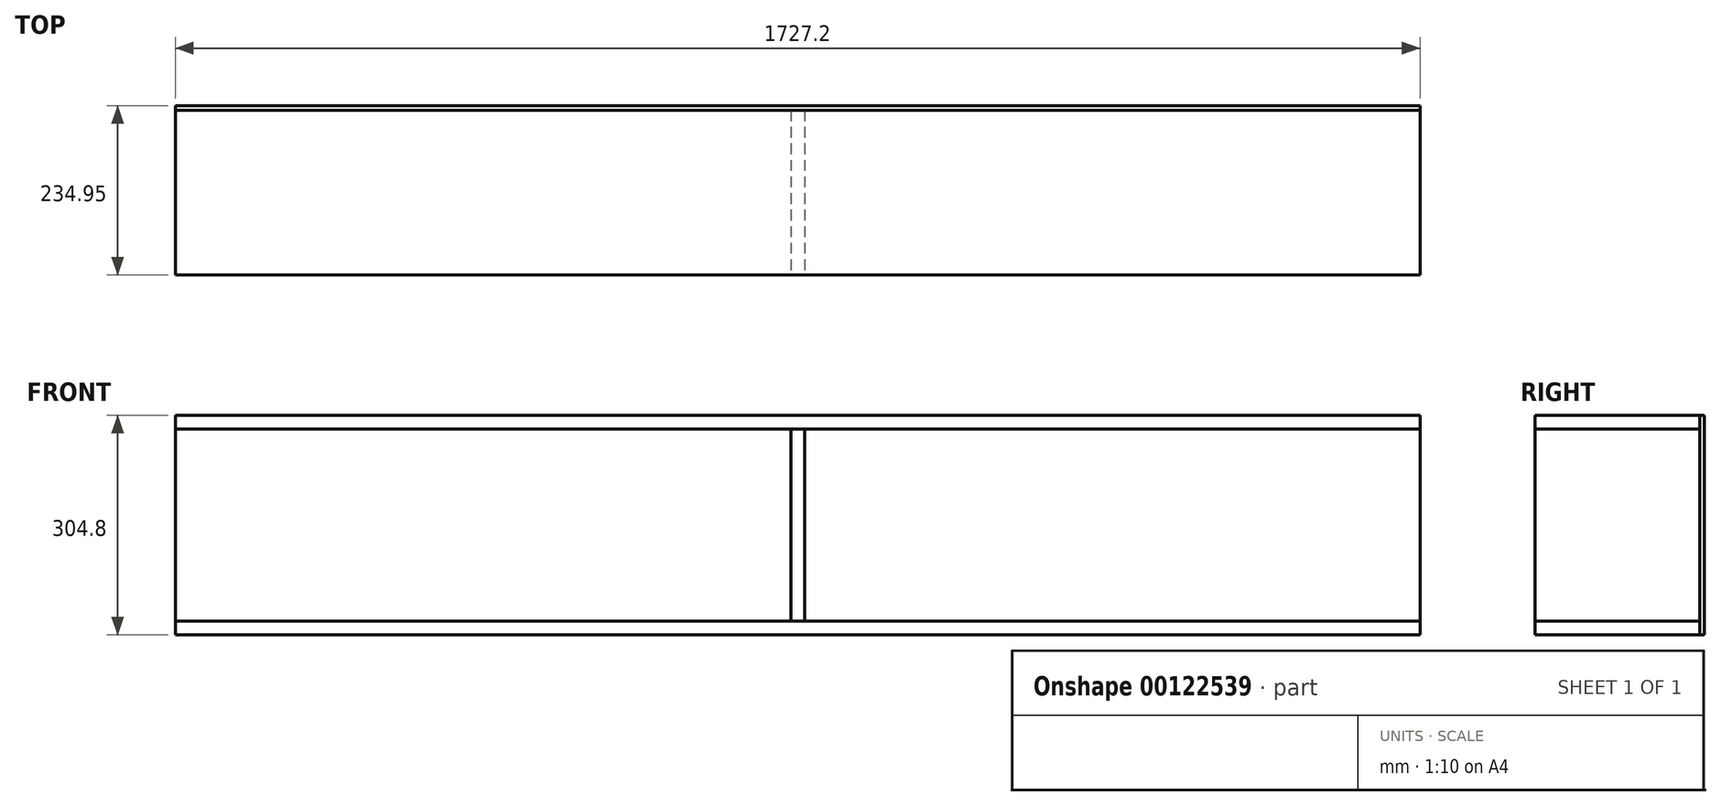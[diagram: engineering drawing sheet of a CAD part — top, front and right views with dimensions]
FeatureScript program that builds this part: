
annotation { "Feature Type Name" : "Feature", "Feature Type Description" : "" }
export const myFeature = defineFeature(function(context is Context, id is Id, definition is map)
    precondition{}
    {
        {
            var Q0;
            Q0=qCreatedBy(makeId("Front.planeOp"),FACE);
            var sketch = newSketch(context, id + "F0", { "sketchPlane" : qUnion([Q0])});
            skLineSegment(sketch, "E0.bottom", {"start": v(863.6, 152.4) * mm, "end": v(-863.6, 152.4) * mm});
            skLineSegment(sketch, "E0.top", {"start": v(863.6, -152.4) * mm, "end": v(-863.6, -152.4) * mm});
            skLineSegment(sketch, "E0.left", {"start": v(863.6, 152.4) * mm, "end": v(863.6, -152.4) * mm});
            skLineSegment(sketch, "E0.right", {"start": v(-863.6, 152.4) * mm, "end": v(-863.6, -152.4) * mm});
            skPoint(sketch, "E0.middle", {"position": v(0, 0) * mm});
            skSolve(sketch);
        }
        {
            var Q0;
            Q0=makeQuery(id+"F0.imprint","IMPRINT",FACE,{"disambiguationData":[TD([[makeQuery(id+"F0.imprint","IMPRINT",EDGE,{"derivedFrom":sQuery(id+"F0.wireOp",EDGE,"xGEZbSv2-N8Y7-1Q99-uAtn-VSa03LQQEVOZ.bottom")}),-1.0]])]});
            var Q1;
            Q1=makeQuery(id+"F0.imprint","IMPRINT",FACE,{"disambiguationData":[TD([[makeQuery(id+"F0.imprint","IMPRINT",EDGE,{"derivedFrom":sQuery(id+"F0.wireOp",EDGE,"E0.bottom")}),1.0]])]});
            var Q2;
            Q2=sQuery(id+"F0.wireOp",EDGE,"xGEZbSv2-N8Y7-1Q99-uAtn-VSa03LQQEVOZ.right");
            var Q3;
            Q3=sQuery(id+"F0.wireOp",EDGE,"xGEZbSv2-N8Y7-1Q99-uAtn-VSa03LQQEVOZ.left");
            extrude(context, id + "F1", {"entities" : qUnion([Q0, Q1]), "surfaceEntities" : qUnion([Q2, Q3]), "oppositeDirection" : true, "depth" : 6.35 * mm});
        }
        {
            var Q0;
            Q0=makeQuery(id+"F1.opExtrude","CAP_FACE",FACE,{"disambiguationData":[OSD([sQuery(id+"F0.wireOp",EDGE,"E0.bottom"),sQuery(id+"F0.wireOp",EDGE,"E0.top"),sQuery(id+"F0.wireOp",EDGE,"E0.left"),sQuery(id+"F0.wireOp",EDGE,"E0.right")])],"isStart":true});
            var sketch = newSketch(context, id + "F2", { "sketchPlane" : qUnion([Q0])});
            skLineSegment(sketch, "E1.0", {"start": v(863.6, 152.4) * mm, "end": v(-863.6, 152.4) * mm});
            skLineSegment(sketch, "E1.1", {"start": v(863.6, -152.4) * mm, "end": v(-863.6, -152.4) * mm});
            skSolve(sketch);
        }
        {
            var Q0;
            Q0=makeQuery(id+"F2.imprint","IMPRINT",FACE,{"disambiguationData":[TD([[makeQuery(id+"F2.imprint","IMPRINT",EDGE,{"derivedFrom":sQuery(id+"F2.wireOp",EDGE,"E1.0")}),1.0]])]});
            var Q1;
            Q1=sQuery(id+"F2.wireOp",EDGE,"E1.0");
            extrude(context, id + "F3", {"entities" : qUnion([Q0]), "bodyType" : ToolBodyType.SURFACE, "surfaceEntities" : qUnion([Q1]), "depth" : 228.6 * mm});
        }
        {
            var Q0;
            Q0=makeQuery(id+"F3.opExtrude","SWEPT_FACE",FACE,{"disambiguationData":[OSD([sQuery(id+"F2.wireOp",EDGE,"E1.0")])]});
            extrude(context, id + "F4", {"entities" : qUnion([Q0]), "oppositeDirection" : true, "depth" : 19.05 * mm});
        }
        {
            var Q0;
            Q0=makeQuery(id+"F4.opExtrude","SWEPT_BODY",BODY,{"disambiguationData":[OSD([sQuery(id+"F2.wireOp",EDGE,"E1.0")])]});
            var Q1;
            Q1=qCreatedBy(makeId("Top.planeOp"),FACE);
            mirror(context, id + "F5", {"entities" : qUnion([Q0]), "mirrorPlane" : qUnion([Q1])});
        }
        {
            var Q0;
            Q0=qCreatedBy(makeId("Right.planeOp"),FACE);
            var sketch = newSketch(context, id + "F6", { "sketchPlane" : qUnion([Q0])});
            skLineSegment(sketch, "E2.0", {"start": v(0, 133.35) * mm, "end": v(-228.6, 133.35) * mm});
            skLineSegment(sketch, "E3.MirrorCS", {"start": v(0, -133.35) * mm, "end": v(-228.6, -133.35) * mm});
            skLineSegment(sketch, "E4", {"start": v(0, 133.35) * mm, "end": v(0, -133.35) * mm});
            skLineSegment(sketch, "E5", {"start": v(-228.6, -133.35) * mm, "end": v(-228.6, 133.35) * mm});
            skSolve(sketch);
        }
        {
            var Q0;
            Q0=makeQuery(id+"F6.imprint","IMPRINT",FACE,{"disambiguationData":[TD([[makeQuery(id+"F6.imprint","IMPRINT",EDGE,{"derivedFrom":sQuery(id+"F6.wireOp",EDGE,"E2.0")}),1.0]])]});
            extrude(context, id + "F7", {"entities" : qUnion([Q0]), "depth" : 9.52 * mm, "hasSecondDirection" : true, "secondDirectionOppositeDirection" : true, "secondDirectionDepth" : 9.52 * mm});
        }
    });
